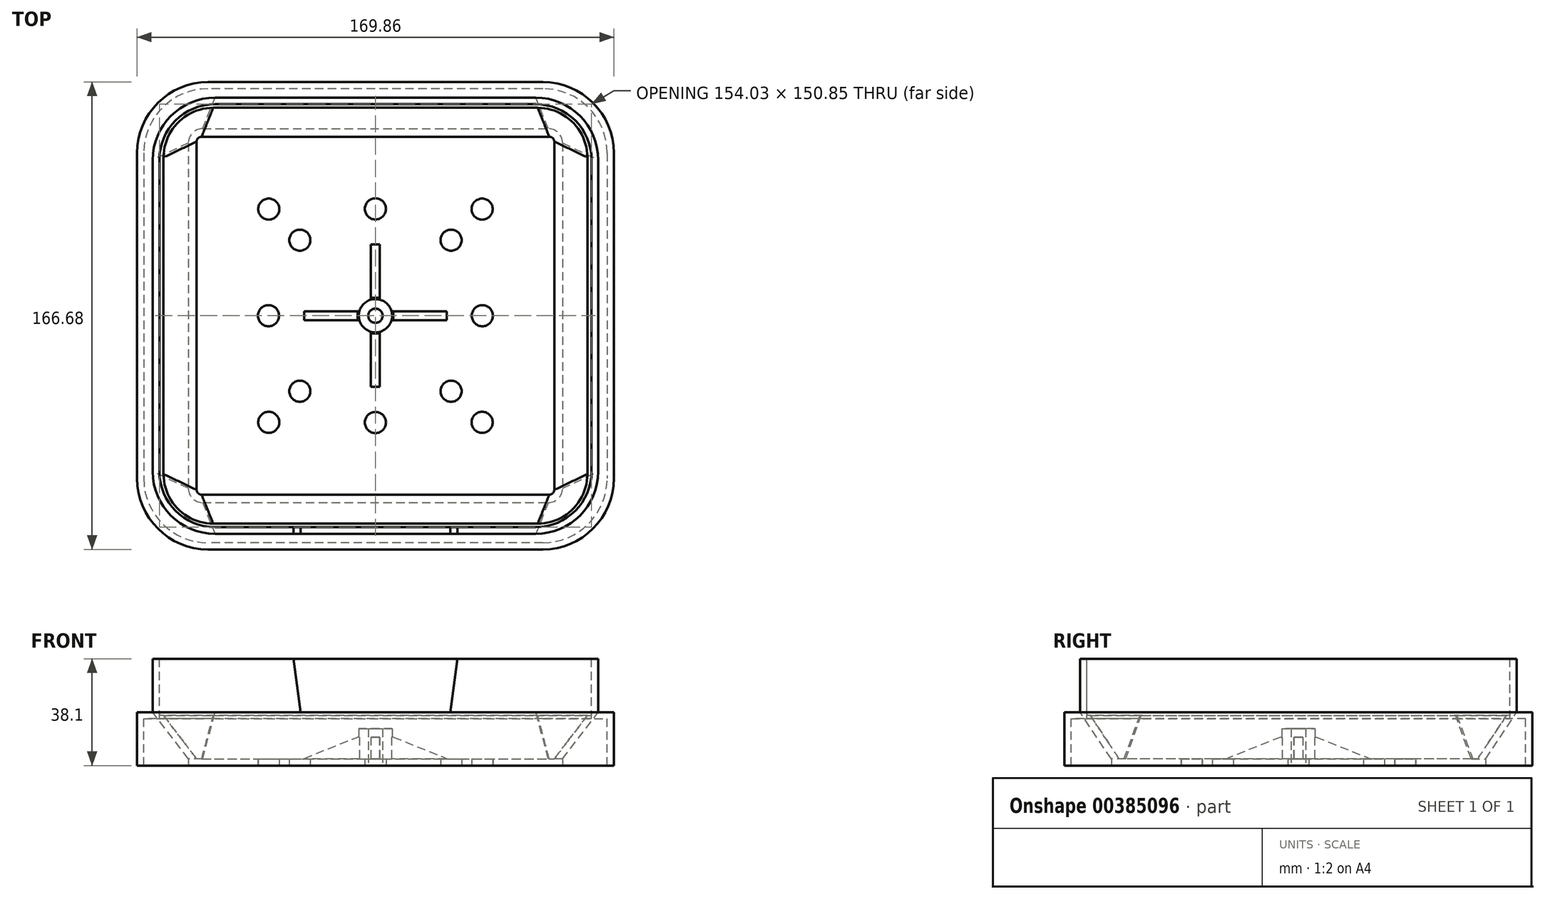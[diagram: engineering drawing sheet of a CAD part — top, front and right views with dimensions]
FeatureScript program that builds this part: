
annotation { "Feature Type Name" : "Feature", "Feature Type Description" : "" }
export const myFeature = defineFeature(function(context is Context, id is Id, definition is map)
    precondition{}
    {
        {
            var Q0;
            Q0=qCreatedBy(makeId("Top.planeOp"),FACE);
            var sketch = newSketch(context, id + "F0", { "sketchPlane" : qUnion([Q0])});
            skLineSegment(sketch, "E0.bottom", {"start": v(59.63, 83.34) * mm, "end": v(-59.63, 83.34) * mm});
            skLineSegment(sketch, "E0.top", {"start": v(59.63, -83.34) * mm, "end": v(-59.63, -83.34) * mm});
            skLineSegment(sketch, "E0.left", {"start": v(84.93, 58.05) * mm, "end": v(84.93, -58.05) * mm});
            skLineSegment(sketch, "E0.right", {"start": v(-84.93, 58.05) * mm, "end": v(-84.93, -58.05) * mm});
            skPoint(sketch, "E0.middle", {"position": v(0, 0) * mm});
            skPoint(sketch, "E1.visualSharp", {"position": v(-84.93, 83.34) * mm});
            skArc(sketch, "E1.filletArc", {"start": v(-59.63, 83.34) * mm, "mid": v(-77.52, 75.93) * mm, "end": v(-84.93, 58.05) * mm});
            skPoint(sketch, "E2.visualSharp", {"position": v(84.93, 83.34) * mm});
            skArc(sketch, "E2.filletArc", {"start": v(84.93, 58.05) * mm, "mid": v(77.52, 75.93) * mm, "end": v(59.63, 83.34) * mm});
            skPoint(sketch, "E3.visualSharp", {"position": v(84.93, -83.34) * mm});
            skArc(sketch, "E3.filletArc", {"start": v(59.63, -83.34) * mm, "mid": v(77.52, -75.93) * mm, "end": v(84.93, -58.05) * mm});
            skPoint(sketch, "E4.visualSharp", {"position": v(-84.93, -83.34) * mm});
            skArc(sketch, "E4.filletArc", {"start": v(-84.93, -58.05) * mm, "mid": v(-77.52, -75.93) * mm, "end": v(-59.63, -83.34) * mm});
            skSolve(sketch);
        }
        {
            var Q0;
            Q0=qCreatedBy(makeId("Top.planeOp"),FACE);
            cPlane(context, id + "F1", {"entities" : qUnion([Q0]), "cplaneType" : CPlaneType.OFFSET, "offset" : 19.05 * mm, "width" : 152.4 * mm, "height" : 152.4 * mm});
        }
        {
            var Q0;
            Q0=qCreatedBy(id+"F1.planeOp",FACE);
            var sketch = newSketch(context, id + "F2", { "sketchPlane" : qUnion([Q0])});
            skLineSegment(sketch, "E5.bottom", {"start": v(57.15, 77.79) * mm, "end": v(-57.15, 77.79) * mm});
            skLineSegment(sketch, "E5.top", {"start": v(57.15, -77.79) * mm, "end": v(-57.15, -77.79) * mm});
            skLineSegment(sketch, "E5.left", {"start": v(79.38, 55.56) * mm, "end": v(79.38, -55.56) * mm});
            skLineSegment(sketch, "E5.right", {"start": v(-79.38, 55.56) * mm, "end": v(-79.38, -55.56) * mm});
            skPoint(sketch, "E5.middle", {"position": v(0, 0) * mm});
            skPoint(sketch, "E6.visualSharp", {"position": v(-79.38, 77.79) * mm});
            skArc(sketch, "E6.filletArc", {"start": v(-57.15, 77.79) * mm, "mid": v(-72.87, 71.28) * mm, "end": v(-79.38, 55.56) * mm});
            skPoint(sketch, "E7.visualSharp", {"position": v(79.38, 77.79) * mm});
            skArc(sketch, "E7.filletArc", {"start": v(79.38, 55.56) * mm, "mid": v(72.87, 71.28) * mm, "end": v(57.15, 77.79) * mm});
            skPoint(sketch, "E8.visualSharp", {"position": v(79.38, -77.79) * mm});
            skArc(sketch, "E8.filletArc", {"start": v(57.15, -77.79) * mm, "mid": v(72.87, -71.28) * mm, "end": v(79.38, -55.56) * mm});
            skPoint(sketch, "E9.visualSharp", {"position": v(-79.38, -77.79) * mm});
            skArc(sketch, "E9.filletArc", {"start": v(-79.38, -55.56) * mm, "mid": v(-72.87, -71.28) * mm, "end": v(-57.15, -77.79) * mm});
            skSolve(sketch);
        }
        {
            var Q0;
            Q0=makeQuery(id+"F0.imprint","IMPRINT",FACE,{"disambiguationData":[TD([[makeQuery(id+"F0.imprint","IMPRINT",EDGE,{"derivedFrom":sQuery(id+"F0.wireOp",EDGE,"E0.bottom")}),1.0]])]});
            extrude(context, id + "F3", {"entities" : qUnion([Q0]), "oppositeDirection" : true, "depth" : 19.05 * mm});
        }
        {
            var Q0;
            Q0=makeQuery(id+"F2.imprint","IMPRINT",FACE,{"disambiguationData":[TD([[makeQuery(id+"F2.imprint","IMPRINT",EDGE,{"derivedFrom":sQuery(id+"F2.wireOp",EDGE,"E5.bottom")}),1.0]])]});
            extrude(context, id + "F4", {"entities" : qUnion([Q0]), "operationType" : NewBodyOperationType.ADD, "endBound" : BoundingType.UP_TO_NEXT, "oppositeDirection" : true, "depth" : 25.4 * mm});
        }
        {
            var Q0;
            Q0=makeQuery(id+"F3.opExtrude","CAP_FACE",FACE,{"disambiguationData":[OSD([sQuery(id+"F0.wireOp",EDGE,"E0.bottom"),sQuery(id+"F0.wireOp",EDGE,"E0.top"),sQuery(id+"F0.wireOp",EDGE,"E0.left"),sQuery(id+"F0.wireOp",EDGE,"E0.right"),sQuery(id+"F0.wireOp",EDGE,"E1.filletArc"),sQuery(id+"F0.wireOp",EDGE,"E2.filletArc"),sQuery(id+"F0.wireOp",EDGE,"E3.filletArc"),sQuery(id+"F0.wireOp",EDGE,"E4.filletArc")])],"isStart":false});
            var Q1;
            Q1=makeQuery(id+"F4.opExtrude","CAP_FACE",FACE,{"disambiguationData":[OSD([sQuery(id+"F2.wireOp",EDGE,"E5.bottom"),sQuery(id+"F2.wireOp",EDGE,"E5.top"),sQuery(id+"F2.wireOp",EDGE,"E5.left"),sQuery(id+"F2.wireOp",EDGE,"E5.right"),sQuery(id+"F2.wireOp",EDGE,"E6.filletArc"),sQuery(id+"F2.wireOp",EDGE,"E7.filletArc"),sQuery(id+"F2.wireOp",EDGE,"E8.filletArc"),sQuery(id+"F2.wireOp",EDGE,"E9.filletArc")])],"isStart":true});
            shell(context, id + "F5", {"entities" : qUnion([Q0, Q1]), "thickness" : 2.36 * mm});
        }
        {
            var Q0;
            Q0=qCreatedBy(makeId("Top.planeOp"),FACE);
            var sketch = newSketch(context, id + "F6", { "sketchPlane" : qUnion([Q0])});
            skLineSegment(sketch, "E10.0", {"start": v(-57.15, -77.79) * mm, "end": v(57.15, -77.79) * mm});
            skLineSegment(sketch, "E10.1", {"start": v(-79.37, 55.56) * mm, "end": v(-79.37, -55.56) * mm});
            skLineSegment(sketch, "E10.2", {"start": v(-57.15, 77.79) * mm, "end": v(57.15, 77.79) * mm});
            skLineSegment(sketch, "E10.3", {"start": v(79.37, 55.56) * mm, "end": v(79.37, -55.56) * mm});
            skArc(sketch, "E11.filletArc", {"start": v(57.15, -77.79) * mm, "mid": v(72.87, -71.28) * mm, "end": v(79.37, -55.56) * mm});
            skArc(sketch, "E12.filletArc", {"start": v(79.37, 55.56) * mm, "mid": v(72.87, 71.28) * mm, "end": v(57.15, 77.79) * mm});
            skArc(sketch, "E13.filletArc", {"start": v(-57.15, 77.79) * mm, "mid": v(-72.87, 71.28) * mm, "end": v(-79.37, 55.56) * mm});
            skArc(sketch, "E14.filletArc", {"start": v(-79.37, -55.56) * mm, "mid": v(-72.87, -71.28) * mm, "end": v(-57.15, -77.79) * mm});
            skSolve(sketch);
        }
        {
            var Q0;
            Q0=makeQuery(id+"F3.opExtrude","CAP_FACE",FACE,{"disambiguationData":[OSD([sQuery(id+"F0.wireOp",EDGE,"E0.bottom"),sQuery(id+"F0.wireOp",EDGE,"E0.top"),sQuery(id+"F0.wireOp",EDGE,"E0.left"),sQuery(id+"F0.wireOp",EDGE,"E0.right"),sQuery(id+"F0.wireOp",EDGE,"E1.filletArc"),sQuery(id+"F0.wireOp",EDGE,"E2.filletArc"),sQuery(id+"F0.wireOp",EDGE,"E3.filletArc"),sQuery(id+"F0.wireOp",EDGE,"E4.filletArc")])],"isStart":false});
            var sketch = newSketch(context, id + "F7", { "sketchPlane" : qUnion([Q0])});
            skLineSegment(sketch, "E15.bottom", {"start": v(-61.6, -66.68) * mm, "end": v(61.6, -66.68) * mm});
            skLineSegment(sketch, "E15.top", {"start": v(-61.6, 66.68) * mm, "end": v(61.6, 66.68) * mm});
            skLineSegment(sketch, "E15.left", {"start": v(-66.68, -61.6) * mm, "end": v(-66.68, 61.6) * mm});
            skLineSegment(sketch, "E15.right", {"start": v(66.68, -61.6) * mm, "end": v(66.68, 61.6) * mm});
            skPoint(sketch, "E15.middle", {"position": v(0, 0) * mm});
            skPoint(sketch, "E16.visualSharp", {"position": v(-66.68, 66.68) * mm});
            skArc(sketch, "E16.filletArc", {"start": v(-61.6, 66.68) * mm, "mid": v(-65.19, 65.19) * mm, "end": v(-66.68, 61.6) * mm});
            skPoint(sketch, "E17.visualSharp", {"position": v(66.68, 66.68) * mm});
            skArc(sketch, "E17.filletArc", {"start": v(66.68, 61.6) * mm, "mid": v(65.19, 65.19) * mm, "end": v(61.6, 66.68) * mm});
            skPoint(sketch, "E18.visualSharp", {"position": v(66.68, -66.68) * mm});
            skArc(sketch, "E18.filletArc", {"start": v(61.6, -66.68) * mm, "mid": v(65.19, -65.19) * mm, "end": v(66.68, -61.6) * mm});
            skPoint(sketch, "E19.visualSharp", {"position": v(-66.68, -66.68) * mm});
            skArc(sketch, "E19.filletArc", {"start": v(-66.68, -61.6) * mm, "mid": v(-65.19, -65.19) * mm, "end": v(-61.6, -66.68) * mm});
            skSolve(sketch);
        }
        {
            var Q0;
            Q0=makeQuery(id+"F7.imprint","IMPRINT",FACE,{"disambiguationData":[TD([[makeQuery(id+"F7.imprint","IMPRINT",EDGE,{"derivedFrom":sQuery(id+"F7.wireOp",EDGE,"E15.bottom")}),1.0]])]});
            extrude(context, id + "F8", {"entities" : qUnion([Q0]), "oppositeDirection" : true, "depth" : 2.36 * mm});
        }
        {
            var Q0;
            Q0=makeQuery(id+"F6.imprint","IMPRINT",FACE,{"disambiguationData":[TD([[makeQuery(id+"F6.imprint","IMPRINT",EDGE,{"derivedFrom":sQuery(id+"F6.wireOp",EDGE,"E10.0")}),1.0]])]});
            extrude(context, id + "F9", {"entities" : qUnion([Q0]), "operationType" : NewBodyOperationType.ADD, "depth" : 2.36 * mm, "symmetric" : true});
        }
        {
            var Q1;
            Q1=makeQuery(id+"F8.opExtrude","CAP_FACE",FACE,{"disambiguationData":[OSD([sQuery(id+"F7.wireOp",EDGE,"E15.bottom"),sQuery(id+"F7.wireOp",EDGE,"E15.top"),sQuery(id+"F7.wireOp",EDGE,"E15.left"),sQuery(id+"F7.wireOp",EDGE,"E15.right"),sQuery(id+"F7.wireOp",EDGE,"E16.filletArc"),sQuery(id+"F7.wireOp",EDGE,"E17.filletArc"),sQuery(id+"F7.wireOp",EDGE,"E18.filletArc"),sQuery(id+"F7.wireOp",EDGE,"E19.filletArc")])],"isStart":false});
            var Q2;
            Q2 = qSketchRegion(id + "F6", true);
            loft(context, id + "F10", {"sheetProfilesArray" : [{ "sheetProfileEntities" : qUnion([Q1]) }, { "sheetProfileEntities" : qUnion([Q2]) }]});
        }
        {
            var Q0;
            Q0=makeQuery(id+"F10.opLoft","CAP_FACE",FACE,{"disambiguationData":[OSD([makeQuery(id+"F6.imprint","IMPRINT",FACE,{"disambiguationData":[TD([[makeQuery(id+"F6.imprint","IMPRINT",EDGE,{"derivedFrom":sQuery(id+"F6.wireOp",EDGE,"E10.0")}),1.0]])]})])],"isStart":true});
            var Q1;
            Q1=makeQuery(id+"F10.opLoft","CAP_FACE",FACE,{"disambiguationData":[OSD([sQuery(id+"F7.wireOp",EDGE,"E15.bottom"),sQuery(id+"F7.wireOp",EDGE,"E15.top"),sQuery(id+"F7.wireOp",EDGE,"E15.left"),sQuery(id+"F7.wireOp",EDGE,"E15.right"),sQuery(id+"F7.wireOp",EDGE,"E16.filletArc"),sQuery(id+"F7.wireOp",EDGE,"E17.filletArc"),sQuery(id+"F7.wireOp",EDGE,"E18.filletArc"),sQuery(id+"F7.wireOp",EDGE,"E19.filletArc")])],"isStart":true});
            var Q2;
            Q2=makeQuery(id+"F10.opLoft","SWEPT_BODY",BODY,{"disambiguationData":[OSD([makeQuery(id+"F6.imprint","IMPRINT",FACE,{"disambiguationData":[TD([[makeQuery(id+"F6.imprint","IMPRINT",EDGE,{"derivedFrom":sQuery(id+"F6.wireOp",EDGE,"E10.0")}),1.0]])]}),sQuery(id+"F7.wireOp",EDGE,"E15.bottom"),sQuery(id+"F7.wireOp",EDGE,"E15.top"),sQuery(id+"F7.wireOp",EDGE,"E15.left"),sQuery(id+"F7.wireOp",EDGE,"E15.right"),sQuery(id+"F7.wireOp",EDGE,"E16.filletArc"),sQuery(id+"F7.wireOp",EDGE,"E17.filletArc"),sQuery(id+"F7.wireOp",EDGE,"E18.filletArc"),sQuery(id+"F7.wireOp",EDGE,"E19.filletArc")])]});
            shell(context, id + "F11", {"entities" : qUnion([Q0, Q1]), "parts" : qUnion([Q2]), "thickness" : 2.36 * mm});
        }
        {
            var Q0;
            Q0=makeQuery(id+"F9.opExtrude","CAP_FACE",FACE,{"disambiguationData":[OSD([sQuery(id+"F6.wireOp",EDGE,"E10.0"),sQuery(id+"F6.wireOp",EDGE,"E10.1"),sQuery(id+"F6.wireOp",EDGE,"E10.2"),sQuery(id+"F6.wireOp",EDGE,"E10.3"),sQuery(id+"F6.wireOp",EDGE,"E11.filletArc"),sQuery(id+"F6.wireOp",EDGE,"E12.filletArc"),sQuery(id+"F6.wireOp",EDGE,"E13.filletArc"),sQuery(id+"F6.wireOp",EDGE,"E14.filletArc")])],"isStart":true});
            extrude(context, id + "F12", {"entities" : qUnion([Q0]), "operationType" : NewBodyOperationType.REMOVE, "oppositeDirection" : true, "depth" : 25.4 * mm});
        }
        {
            var Q0;
            Q0=makeQuery(id+"F8.opExtrude","CAP_FACE",FACE,{"disambiguationData":[OSD([sQuery(id+"F7.wireOp",EDGE,"E15.bottom"),sQuery(id+"F7.wireOp",EDGE,"E15.top"),sQuery(id+"F7.wireOp",EDGE,"E15.left"),sQuery(id+"F7.wireOp",EDGE,"E15.right"),sQuery(id+"F7.wireOp",EDGE,"E16.filletArc"),sQuery(id+"F7.wireOp",EDGE,"E17.filletArc"),sQuery(id+"F7.wireOp",EDGE,"E18.filletArc"),sQuery(id+"F7.wireOp",EDGE,"E19.filletArc")])],"isStart":false});
            var sketch = newSketch(context, id + "F13", { "sketchPlane" : qUnion([Q0])});
            skCircle(sketch, "E20", {"center": v(-26.94, 26.94) * mm, "radius": 3.76 * mm});
            skCircle(sketch, "E21.1.0", {"center": v(-38.1, 0) * mm, "radius": 3.76 * mm});
            skCircle(sketch, "E21.2.0", {"center": v(-26.94, -26.94) * mm, "radius": 3.76 * mm});
            skPoint(sketch, "E21.center", {"position": v(0, 0) * mm});
            skCircle(sketch, "E22.1.3.0", {"center": v(0, -38.1) * mm, "radius": 3.76 * mm});
            skCircle(sketch, "E22.1.4.0", {"center": v(26.94, -26.94) * mm, "radius": 3.76 * mm});
            skCircle(sketch, "E22.1.5.0", {"center": v(38.1, 0) * mm, "radius": 3.76 * mm});
            skCircle(sketch, "E22.1.6.0", {"center": v(26.94, 26.94) * mm, "radius": 3.76 * mm});
            skCircle(sketch, "E22.1.7.0", {"center": v(0, 38.1) * mm, "radius": 3.76 * mm});
            skCircle(sketch, "E23", {"center": v(0, 0) * mm, "radius": 38.1 * mm});
            skLineSegment(sketch, "E24", {"start": v(0, 0) * mm, "end": v(91, 0) * mm});
            skLineSegment(sketch, "E25", {"start": v(0, 0) * mm, "end": v(38.02, 38.02) * mm});
            skCircle(sketch, "E26", {"center": v(38.02, 38.02) * mm, "radius": 3.76 * mm});
            skCircle(sketch, "E27.1.0", {"center": v(-38.02, 38.02) * mm, "radius": 3.76 * mm});
            skCircle(sketch, "E27.2.0", {"center": v(-38.02, -38.02) * mm, "radius": 3.76 * mm});
            skCircle(sketch, "E28.1.3.0", {"center": v(38.02, -38.02) * mm, "radius": 3.76 * mm});
            skSolve(sketch);
        }
        {
            var Q0;
            Q0=sQuery(id+"F13.wireOp",VERTEX,"E27.2.0.center");
            var Q1;
            Q1=sQuery(id+"F13.wireOp",VERTEX,"E21.2.0.center");
            var Q2;
            Q2=sQuery(id+"F13.wireOp",VERTEX,"E22.1.3.0.center");
            var Q3;
            Q3=sQuery(id+"F13.wireOp",VERTEX,"E22.1.4.0.center");
            var Q4;
            Q4=sQuery(id+"F13.wireOp",VERTEX,"E28.1.3.0.center");
            var Q5;
            Q5=sQuery(id+"F13.wireOp",VERTEX,"E22.1.5.0.center");
            var Q6;
            Q6=sQuery(id+"F13.wireOp",VERTEX,"E22.1.6.0.center");
            var Q7;
            Q7=sQuery(id+"F13.wireOp",VERTEX,"E25.end");
            var Q8;
            Q8=sQuery(id+"F13.wireOp",VERTEX,"E22.1.7.0.center");
            var Q9;
            Q9=sQuery(id+"F13.wireOp",VERTEX,"E20.center");
            var Q10;
            Q10=sQuery(id+"F13.wireOp",VERTEX,"E21.1.0.center");
            var Q11;
            Q11=sQuery(id+"F13.wireOp",VERTEX,"E27.1.0.center");
            var Q12;
            Q12=makeQuery(id+"F8.opExtrude","SWEPT_BODY",BODY,{"disambiguationData":[OSD([sQuery(id+"F7.wireOp",EDGE,"E15.bottom"),sQuery(id+"F7.wireOp",EDGE,"E15.top"),sQuery(id+"F7.wireOp",EDGE,"E15.left"),sQuery(id+"F7.wireOp",EDGE,"E15.right"),sQuery(id+"F7.wireOp",EDGE,"E16.filletArc"),sQuery(id+"F7.wireOp",EDGE,"E17.filletArc"),sQuery(id+"F7.wireOp",EDGE,"E18.filletArc"),sQuery(id+"F7.wireOp",EDGE,"E19.filletArc")])]});
            hole(context, id + "F14", {"style" : HoleStyle.SIMPLE, "endStyle" : HoleEndStyle.THROUGH, "holeDiameter" : 7.52 * mm, "isTappedThrough" : true, "tappedDepth" : 12.7 * mm, "tapClearance" : 3, "locations" : qUnion([Q0, Q1, Q2, Q3, Q4, Q5, Q6, Q7, Q8, Q9, Q10, Q11]), "scope" : qUnion([Q12])});
        }
        {
            var Q0;
            Q0=makeQuery(id+"F4.opExtrude","SWEPT_FACE",FACE,{"disambiguationData":[OSD([sQuery(id+"F2.wireOp",EDGE,"E5.top")])]});
            var sketch = newSketch(context, id + "F15", { "sketchPlane" : qUnion([Q0])});
            skLineSegment(sketch, "E29", {"start": v(0, 0) * mm, "end": v(26.67, 0) * mm});
            skLineSegment(sketch, "E30", {"start": v(26.67, 0) * mm, "end": v(29.21, 19.05) * mm});
            skLineSegment(sketch, "E31", {"start": v(29.21, 19.05) * mm, "end": v(0, 19.05) * mm});
            skLineSegment(sketch, "E32", {"start": v(-29.2, 19.05) * mm, "end": v(-26.67, 0) * mm});
            skLineSegment(sketch, "E33", {"start": v(-26.67, 0) * mm, "end": v(0, 0) * mm});
            skLineSegment(sketch, "E34", {"start": v(0, 19.05) * mm, "end": v(-29.21, 19.05) * mm});
            skSolve(sketch);
        }
        {
            var Q0;
            Q0=makeQuery(id+"F15.imprint","IMPRINT",FACE,{"disambiguationData":[TD([[makeQuery(id+"F15.imprint","IMPRINT",EDGE,{"derivedFrom":sQuery(id+"F15.wireOp",EDGE,"E29")}),1.0]])]});
            extrude(context, id + "F16", {"entities" : qUnion([Q0]), "operationType" : NewBodyOperationType.REMOVE, "endBound" : BoundingType.UP_TO_NEXT, "oppositeDirection" : true, "depth" : 25.4 * mm});
        }
        {
            var Q0;
            Q0=makeQuery(id+"F8.opExtrude","CAP_FACE",FACE,{"disambiguationData":[OSD([sQuery(id+"F7.wireOp",EDGE,"E15.bottom"),sQuery(id+"F7.wireOp",EDGE,"E15.top"),sQuery(id+"F7.wireOp",EDGE,"E15.left"),sQuery(id+"F7.wireOp",EDGE,"E15.right"),sQuery(id+"F7.wireOp",EDGE,"E16.filletArc"),sQuery(id+"F7.wireOp",EDGE,"E17.filletArc"),sQuery(id+"F7.wireOp",EDGE,"E18.filletArc"),sQuery(id+"F7.wireOp",EDGE,"E19.filletArc")])],"isStart":false});
            var sketch = newSketch(context, id + "F17", { "sketchPlane" : qUnion([Q0])});
            skCircle(sketch, "E35", {"center": v(0, 0) * mm, "radius": 5.94 * mm});
            skLineSegment(sketch, "E36.bottom", {"start": v(1.59, -25.4) * mm, "end": v(-1.59, -25.4) * mm});
            skLineSegment(sketch, "E36.top", {"start": v(1.59, 25.4) * mm, "end": v(-1.59, 25.4) * mm});
            skLineSegment(sketch, "E36.left", {"start": v(1.59, -25.4) * mm, "end": v(1.59, -5.73) * mm});
            skLineSegment(sketch, "E36.right", {"start": v(-1.59, -25.4) * mm, "end": v(-1.59, -5.73) * mm});
            skLineSegment(sketch, "E37.bottom", {"start": v(25.4, -1.59) * mm, "end": v(5.73, -1.59) * mm});
            skLineSegment(sketch, "E37.top", {"start": v(25.4, 1.59) * mm, "end": v(5.73, 1.59) * mm});
            skLineSegment(sketch, "E37.left", {"start": v(25.4, -1.59) * mm, "end": v(25.4, 1.59) * mm});
            skLineSegment(sketch, "E37.right", {"start": v(-25.4, -1.59) * mm, "end": v(-25.4, 1.59) * mm});
            skLineSegment(sketch, "E38.trimOffspring", {"start": v(-1.59, 5.73) * mm, "end": v(-1.59, 25.4) * mm});
            skLineSegment(sketch, "E39.trimOffspring", {"start": v(1.59, 5.73) * mm, "end": v(1.59, 25.4) * mm});
            skLineSegment(sketch, "E40.trimOffspring", {"start": v(-5.73, -1.59) * mm, "end": v(-25.4, -1.59) * mm});
            skLineSegment(sketch, "E41.trimOffspring", {"start": v(-5.73, 1.59) * mm, "end": v(-25.4, 1.59) * mm});
            skSolve(sketch);
        }
        {
            var Q0;
            Q0=makeQuery(id+"F17.imprint","IMPRINT",FACE,{"disambiguationData":[TD([[makeQuery(id+"F17.imprint","IMPRINT",EDGE,{"derivedFrom":sQuery(id+"F17.wireOp",EDGE,"E35")}),1.0]])]});
            extrude(context, id + "F18", {"entities" : qUnion([Q0]), "operationType" : NewBodyOperationType.ADD, "depth" : 10.8 * mm});
        }
        {
            var Q0;
            Q0=makeQuery(id+"F18.opExtrude","CAP_FACE",FACE,{"disambiguationData":[OSD([sQuery(id+"F17.wireOp",EDGE,"E35")])],"isStart":false});
            var sketch = newSketch(context, id + "F19", { "sketchPlane" : qUnion([Q0])});
            skCircle(sketch, "E42.0.0", {"center": v(0, 0) * mm, "radius": 5.94 * mm});
            skSolve(sketch);
        }
        {
            var Q0;
            Q0=sQuery(id+"F19.wireOp",VERTEX,"E42.0.0.center");
            var Q1;
            Q1=makeQuery(id+"F8.opExtrude","SWEPT_BODY",BODY,{"disambiguationData":[OSD([sQuery(id+"F7.wireOp",EDGE,"E15.bottom"),sQuery(id+"F7.wireOp",EDGE,"E15.top"),sQuery(id+"F7.wireOp",EDGE,"E15.left"),sQuery(id+"F7.wireOp",EDGE,"E15.right"),sQuery(id+"F7.wireOp",EDGE,"E16.filletArc"),sQuery(id+"F7.wireOp",EDGE,"E17.filletArc"),sQuery(id+"F7.wireOp",EDGE,"E18.filletArc"),sQuery(id+"F7.wireOp",EDGE,"E19.filletArc")])]});
            hole(context, id + "F20", {"style" : HoleStyle.SIMPLE, "endStyle" : HoleEndStyle.THROUGH, "standardTappedOrClearance" : lookupTablePath({ "standard" : "ANSI", "engagement" : "75%", "pitch" : "20 tpi", "size" : "1/4", "type" : "Tapped" }), "standardBlindInLast" : lookupTablePath({ "standard" : "ANSI", "engagement" : "75%", "pitch" : "20 tpi", "size" : "1/4", "type" : "Tapped" }), "holeDiameter" : 5.1 * mm, "showTappedDepth" : true, "isTappedThrough" : true, "tappedDepth" : 12.7 * mm, "tapClearance" : 3, "locations" : qUnion([Q0]), "scope" : qUnion([Q1]), "majorDiameter" : 6.35 * mm});
        }
        {
            var Q0;
            Q0=makeQuery(id+"F17.imprint","IMPRINT",FACE,{"disambiguationData":[TD([[makeQuery(id+"F17.imprint","IMPRINT",EDGE,{"derivedFrom":sQuery(id+"F17.wireOp",EDGE,"E37.right")}),-1.0]])]});
            var Q1;
            Q1=makeQuery(id+"F17.imprint","IMPRINT",FACE,{"disambiguationData":[TD([[makeQuery(id+"F17.imprint","IMPRINT",EDGE,{"derivedFrom":sQuery(id+"F17.wireOp",EDGE,"E36.bottom")}),-1.0]])]});
            var Q2;
            {var subQ0=sQuery(id+"F17.wireOp",EDGE,"E37.bottom");Q2=makeQuery(id+"F17.imprint","IMPRINT",FACE,{"disambiguationData":[TD([[makeQuery(id+"F17.imprint","IMPRINT",EDGE,{"derivedFrom":subQ0}),-1.0]])]});}
            var Q3;
            Q3=makeQuery(id+"F17.imprint","IMPRINT",FACE,{"disambiguationData":[TD([[makeQuery(id+"F17.imprint","IMPRINT",EDGE,{"derivedFrom":sQuery(id+"F17.wireOp",EDGE,"E36.top")}),1.0]])]});
            extrude(context, id + "F21", {"entities" : qUnion([Q0, Q1, Q2, Q3]), "operationType" : NewBodyOperationType.ADD, "depth" : 7.8 * mm});
        }
        {
            var Q0;
            Q0=makeQuery(id+"F21.opExtrude","CAP_EDGE",EDGE,{"disambiguationData":[OSD([sQuery(id+"F17.wireOp",EDGE,"E37.right")])],"isStart":false});
            var Q1;
            Q1=makeQuery(id+"F21.opExtrude","CAP_EDGE",EDGE,{"disambiguationData":[OSD([sQuery(id+"F17.wireOp",EDGE,"E36.bottom")])],"isStart":false});
            chamfer(context, id + "F22", {"entities" : qUnion([Q0, Q1]), "chamferType" : ChamferType.TWO_OFFSETS, "width1" : 7.62 * mm, "oppositeDirection" : false, "width2" : 19.05 * mm});
        }
        {
            var Q0;
            Q0=makeQuery(id+"F21.opExtrude","CAP_EDGE",EDGE,{"disambiguationData":[OSD([sQuery(id+"F17.wireOp",EDGE,"E36.top")])],"isStart":false});
            var Q1;
            Q1=makeQuery(id+"F21.opExtrude","CAP_EDGE",EDGE,{"disambiguationData":[OSD([sQuery(id+"F17.wireOp",EDGE,"E37.left")])],"isStart":false});
            chamfer(context, id + "F23", {"entities" : qUnion([Q0, Q1]), "chamferType" : ChamferType.TWO_OFFSETS, "width1" : 19.05 * mm, "oppositeDirection" : false, "width2" : 7.62 * mm, "tangentPropagation" : true});
        }
    });
